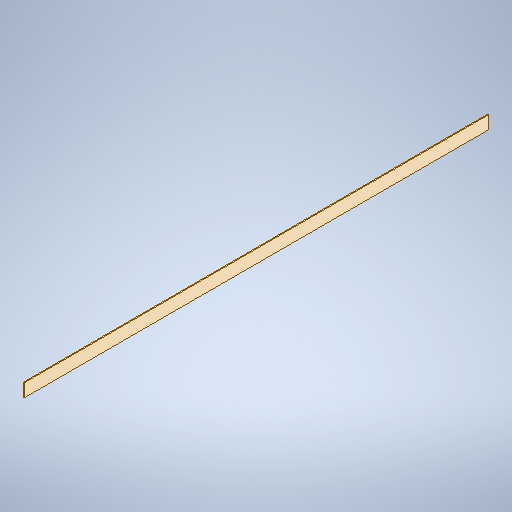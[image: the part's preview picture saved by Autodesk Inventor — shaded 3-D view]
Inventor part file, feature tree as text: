
AUTODESK INVENTOR PART (.ipt)
format: ipt  version: 2025 (Build 290162010, 162A)  size: 251,904 bytes
history: native  units: in
note: dims shown in document units (in); Inventor stores cm internally (conversion verified against a paired STEP export)
features: extrude x1, sketch x1
ambient origin geometry x8: Origin, YZ Plane, XZ Plane, XY Plane, X Axis, Y Axis, Z Axis, Center Point
bodies: Solid1 (feature_tree)
feature tree (2):
  extrude  "Extrusion1"  Depth=3.5in
  sketch  "Sketch1"  dims[d0=0.25in d1=3.5in d2=125.0in d3=0.0in]
